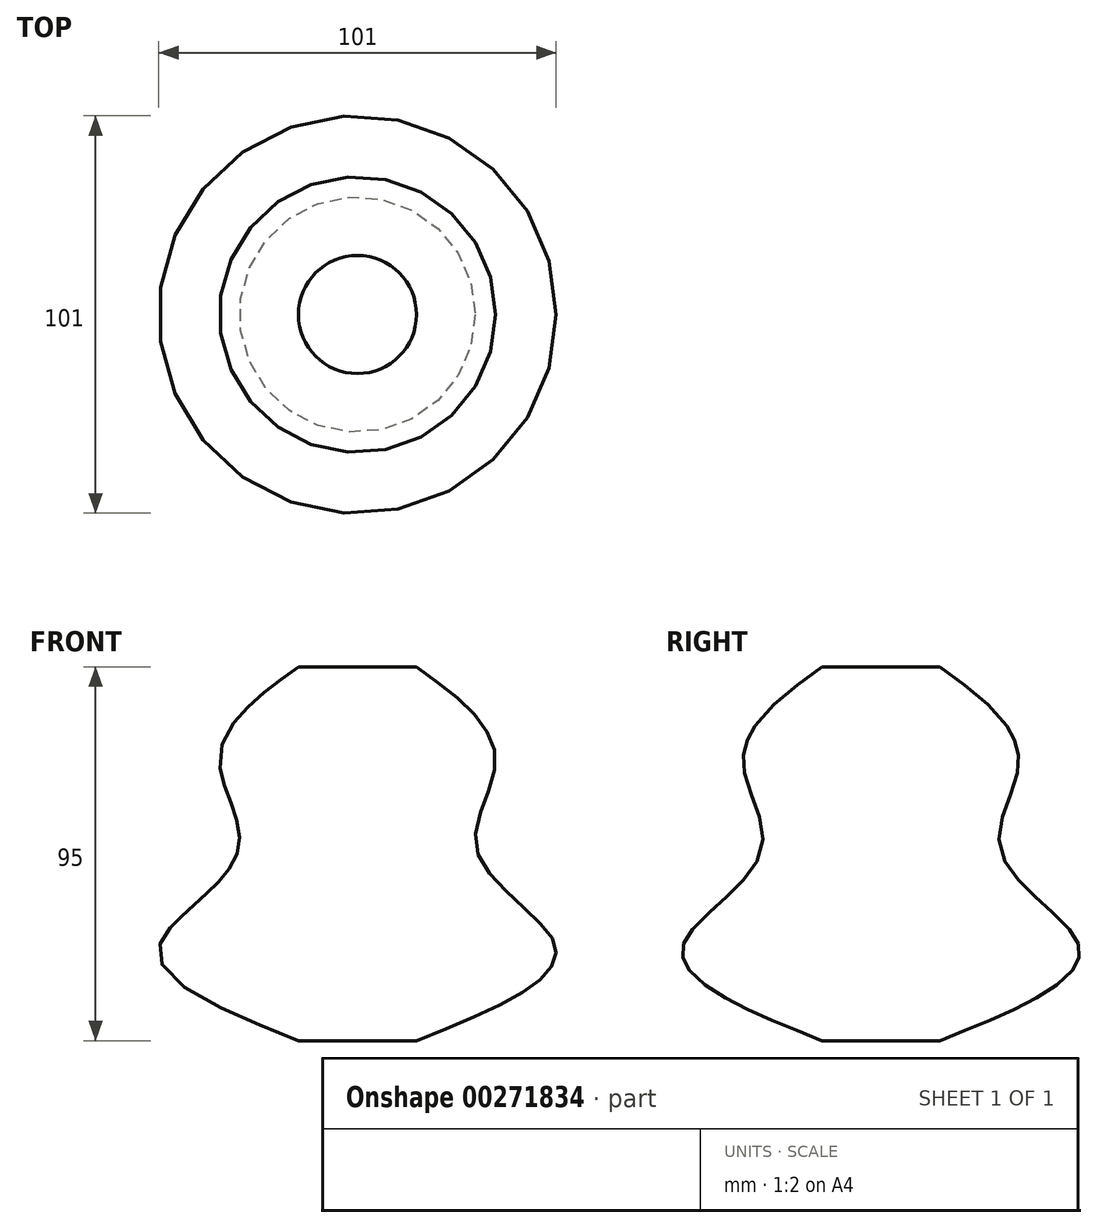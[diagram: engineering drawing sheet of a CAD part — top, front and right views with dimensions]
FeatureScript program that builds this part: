
annotation { "Feature Type Name" : "Feature", "Feature Type Description" : "" }
export const myFeature = defineFeature(function(context is Context, id is Id, definition is map)
    precondition{}
    {
        {
            var Q0;
            Q0=qCreatedBy(makeId("Top.planeOp"),FACE);
            var sketch = newSketch(context, id + "F0", { "sketchPlane" : qUnion([Q0])});
            skCircle(sketch, "E0", {"center": v(0, 0) * mm, "radius": 30 * mm});
            skSolve(sketch);
        }
        {
            var Q0;
            Q0=qCreatedBy(makeId("Top.planeOp"),FACE);
            cPlane(context, id + "F1", {"entities" : qUnion([Q0]), "cplaneType" : CPlaneType.OFFSET, "offset" : 20 * mm, "width" : 150 * mm, "height" : 150 * mm});
        }
        {
            var Q0;
            Q0=qCreatedBy(id+"F1.planeOp",FACE);
            var sketch = newSketch(context, id + "F2", { "sketchPlane" : qUnion([Q0])});
            skCircle(sketch, "E1", {"center": v(0, 0) * mm, "radius": 35 * mm});
            skSolve(sketch);
        }
        {
            var Q0;
            Q0=qCreatedBy(id+"F1.planeOp",FACE);
            cPlane(context, id + "F3", {"entities" : qUnion([Q0]), "cplaneType" : CPlaneType.OFFSET, "offset" : 25 * mm, "width" : 150 * mm, "height" : 150 * mm});
        }
        {
            var Q0;
            Q0=qCreatedBy(id+"F3.planeOp",FACE);
            var sketch = newSketch(context, id + "F4", { "sketchPlane" : qUnion([Q0])});
            skCircle(sketch, "E2", {"center": v(0, 0) * mm, "radius": 15 * mm});
            skSolve(sketch);
        }
        {
            var Q0;
            Q0=qCreatedBy(makeId("Top.planeOp"),FACE);
            cPlane(context, id + "F5", {"entities" : qUnion([Q0]), "cplaneType" : CPlaneType.OFFSET, "offset" : 25 * mm, "oppositeDirection" : true, "width" : 150 * mm, "height" : 150 * mm});
        }
        {
            var Q0;
            Q0=qCreatedBy(id+"F5.planeOp",FACE);
            cPlane(context, id + "F6", {"entities" : qUnion([Q0]), "cplaneType" : CPlaneType.OFFSET, "offset" : 25 * mm, "oppositeDirection" : true, "width" : 150 * mm, "height" : 150 * mm});
        }
        {
            var Q0;
            Q0=qCreatedBy(id+"F6.planeOp",FACE);
            var sketch = newSketch(context, id + "F7", { "sketchPlane" : qUnion([Q0])});
            skCircle(sketch, "E3", {"center": v(0, 0) * mm, "radius": 15 * mm});
            skSolve(sketch);
        }
        {
            var Q0;
            Q0=qCreatedBy(id+"F5.planeOp",FACE);
            var sketch = newSketch(context, id + "F8", { "sketchPlane" : qUnion([Q0])});
            skCircle(sketch, "E4", {"center": v(0, 0) * mm, "radius": 50 * mm});
            skSolve(sketch);
        }
        {
            var Q0;
            Q0=makeQuery(id+"F4.imprint","IMPRINT",FACE,{"disambiguationData":[TD([[makeQuery(id+"F4.imprint","IMPRINT",EDGE,{"derivedFrom":sQuery(id+"F4.wireOp",EDGE,"E2")}),1.0]])]});
            var Q1;
            Q1=makeQuery(id+"F2.imprint","IMPRINT",FACE,{"disambiguationData":[TD([[makeQuery(id+"F2.imprint","IMPRINT",EDGE,{"derivedFrom":sQuery(id+"F2.wireOp",EDGE,"E1")}),1.0]])]});
            var Q2;
            Q2=makeQuery(id+"F0.imprint","IMPRINT",FACE,{"disambiguationData":[TD([[makeQuery(id+"F0.imprint","IMPRINT",EDGE,{"derivedFrom":sQuery(id+"F0.wireOp",EDGE,"E0")}),1.0]])]});
            var Q3;
            Q3=makeQuery(id+"F8.imprint","IMPRINT",FACE,{"disambiguationData":[TD([[makeQuery(id+"F8.imprint","IMPRINT",EDGE,{"derivedFrom":sQuery(id+"F8.wireOp",EDGE,"E4")}),1.0]])]});
            var Q4;
            Q4=makeQuery(id+"F7.imprint","IMPRINT",FACE,{"disambiguationData":[TD([[makeQuery(id+"F7.imprint","IMPRINT",EDGE,{"derivedFrom":sQuery(id+"F7.wireOp",EDGE,"E3")}),1.0]])]});
            loft(context, id + "F9", {"sheetProfilesArray" : [{ "sheetProfileEntities" : qUnion([Q0]) }, { "sheetProfileEntities" : qUnion([Q1]) }, { "sheetProfileEntities" : qUnion([Q2]) }, { "sheetProfileEntities" : qUnion([Q3]) }, { "sheetProfileEntities" : qUnion([Q4]) }]});
        }
    });
